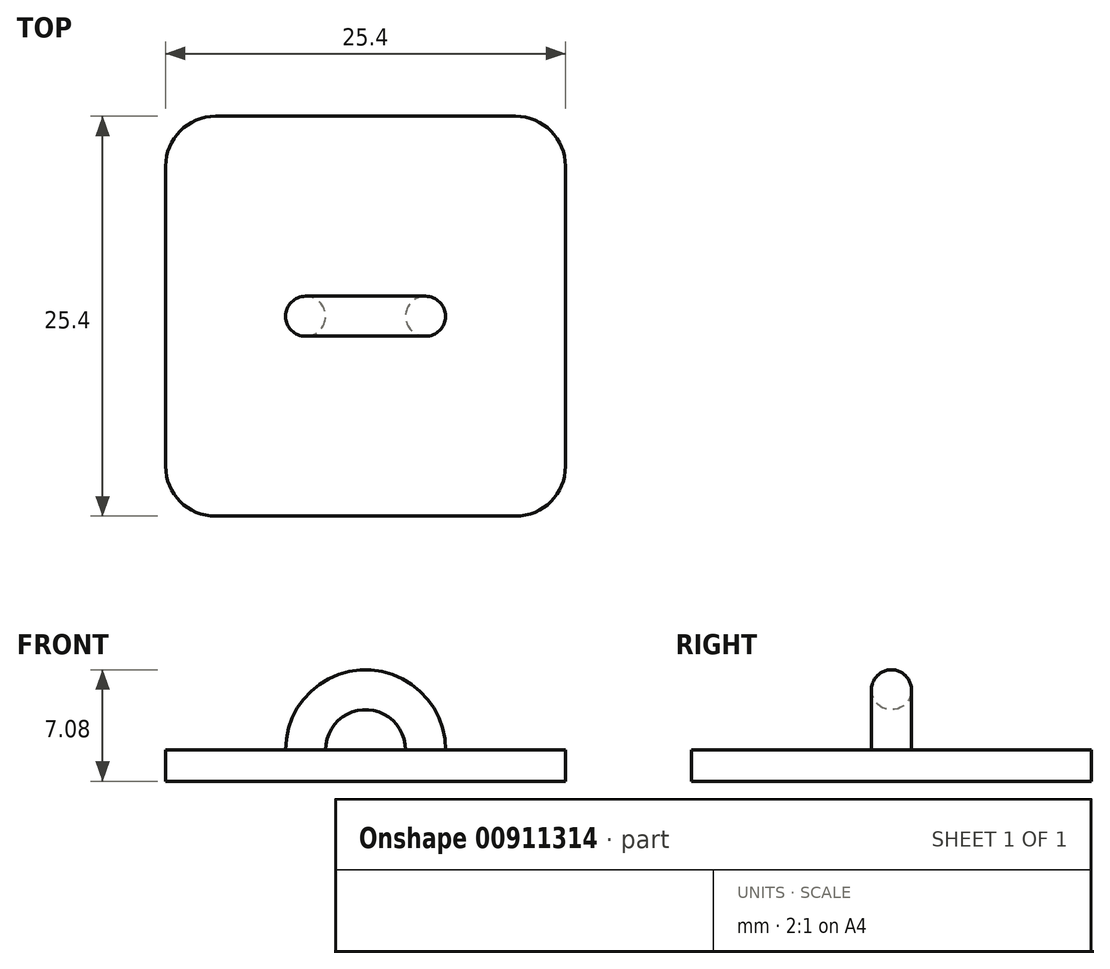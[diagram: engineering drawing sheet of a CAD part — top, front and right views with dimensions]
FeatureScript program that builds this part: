
annotation { "Feature Type Name" : "Feature", "Feature Type Description" : "" }
export const myFeature = defineFeature(function(context is Context, id is Id, definition is map)
    precondition{}
    {
        {
            var Q0;
            Q0=qCreatedBy(makeId("Top.planeOp"),FACE);
            var sketch = newSketch(context, id + "F0", { "sketchPlane" : qUnion([Q0])});
            skLineSegment(sketch, "E0.bottom", {"start": v(12.7, -12.7) * mm, "end": v(-12.7, -12.7) * mm});
            skLineSegment(sketch, "E0.top", {"start": v(12.7, 12.7) * mm, "end": v(-12.7, 12.7) * mm});
            skLineSegment(sketch, "E0.left", {"start": v(12.7, -12.7) * mm, "end": v(12.7, 12.7) * mm});
            skLineSegment(sketch, "E0.right", {"start": v(-12.7, -12.7) * mm, "end": v(-12.7, 12.7) * mm});
            skPoint(sketch, "E0.middle", {"position": v(0, 0) * mm});
            skSolve(sketch);
        }
        {
            var Q0;
            Q0=makeQuery(id+"F0.imprint","IMPRINT",FACE,{"disambiguationData":[TD([[makeQuery(id+"F0.imprint","IMPRINT",EDGE,{"derivedFrom":sQuery(id+"F0.wireOp",EDGE,"E0.bottom")}),-1.0]])]});
            extrude(context, id + "F1", {"entities" : qUnion([Q0]), "depth" : 2 * mm, "offsetDistance" : 25.4 * mm});
        }
        {
            var Q0;
            Q0=makeQuery(id+"F1.opExtrude","CAP_FACE",FACE,{"disambiguationData":[OSD([sQuery(id+"F0.wireOp",EDGE,"E0.bottom"),sQuery(id+"F0.wireOp",EDGE,"E0.top"),sQuery(id+"F0.wireOp",EDGE,"E0.left"),sQuery(id+"F0.wireOp",EDGE,"E0.right")])],"isStart":false});
            var sketch = newSketch(context, id + "F2", { "sketchPlane" : qUnion([Q0])});
            skCircle(sketch, "E1", {"center": v(3.81, 0) * mm, "radius": 1.27 * mm});
            skLineSegment(sketch, "E2", {"start": v(0, 12.7) * mm, "end": v(0, -12.7) * mm, "construction": true});
            skSolve(sketch);
        }
        {
            var Q0;
            Q0=makeQuery(id+"F2.imprint","IMPRINT",FACE,{"disambiguationData":[TD([[makeQuery(id+"F2.imprint","IMPRINT",EDGE,{"derivedFrom":sQuery(id+"F2.wireOp",EDGE,"E1")}),1.0]])]});
            var Q1;
            Q1=sQuery(id+"F2.wireOp",EDGE,"E2");
            revolve(context, id + "F3", {"operationType" : NewBodyOperationType.ADD, "surfaceOperationType" : NewSurfaceOperationType.NEW, "entities" : qUnion([Q0]), "axis" : qUnion([Q1]), "revolveType" : RevolveType.ONE_DIRECTION, "angle" : 180 * degree});
        }
        {
            var Q0;
            Q0=makeQuery(id+"F1.opExtrude","SWEPT_EDGE",EDGE,{"disambiguationData":[OSD([sQuery(id+"F0.wireOp",EDGE,"E0.bottom"),sQuery(id+"F0.wireOp",EDGE,"E0.left")])]});
            var Q1;
            Q1=makeQuery(id+"F1.opExtrude","SWEPT_EDGE",EDGE,{"disambiguationData":[OSD([sQuery(id+"F0.wireOp",EDGE,"E0.bottom"),sQuery(id+"F0.wireOp",EDGE,"E0.right")])]});
            var Q2;
            Q2=makeQuery(id+"F1.opExtrude","SWEPT_EDGE",EDGE,{"disambiguationData":[OSD([sQuery(id+"F0.wireOp",EDGE,"E0.top"),sQuery(id+"F0.wireOp",EDGE,"E0.right")])]});
            var Q3;
            Q3=makeQuery(id+"F1.opExtrude","SWEPT_EDGE",EDGE,{"disambiguationData":[OSD([sQuery(id+"F0.wireOp",EDGE,"E0.top"),sQuery(id+"F0.wireOp",EDGE,"E0.left")])]});
            fillet(context, id + "F4", {"entities" : qUnion([Q0, Q1, Q2, Q3]), "radius" : 3.17 * mm, "tangentPropagation" : true, "allowEdgeOverflow" : false});
        }
    });
